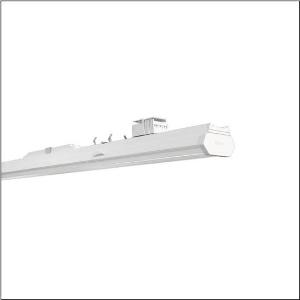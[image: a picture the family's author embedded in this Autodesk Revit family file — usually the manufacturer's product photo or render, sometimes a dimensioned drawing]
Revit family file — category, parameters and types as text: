
# Revit family: licross_r__21_protected_mo_52td12dn48xg_f2a3
name_source: partatom
category: Lighting Fixtures
units: mm (PartAtom-declared; Revit-internal decimal feet)

## family parameters
Cut with Voids When Loaded = No
Host = Face
Light Source = No
Part Type = Normal
Room Calculation Point = No
Round Connector Dimension = Use Diameter
Shared = No

## types (1)
- --- (1 x LED, 8000 lm, 45.3 W, 4000K)
    Apparent Load = 45 VA
    CIE Flux Codes = 73 92 98 99 100
    Color Rendering = 80
    Color Temperature = 4000K
    Default Elevation = 1800 mm
    Description = Licross® 21 Protected MO, luminaire insert, of sheet steel, galvanised, coil coated, white, length: 1.500mm, width: 90mm, height: 103mm, LED rated luminous flux: 8.000lm, light colour: 840, SDCM (Standard Deviation of Colour Matching)MacAdam ≤ 3 SDCM (initial), control gear: DALI 2, with plug, 5-pole, with phase selection, mains connection: 220..240V, AC, 50/60Hz, rated input power: 45W, internal wiring halogen-free, primary light control with lens, of plastic, primary optical cover: cover, of PMMA, light emission: direct distribution, primary light characteristic: symmetric, protection rating (complete): IP54, insulation class (complete): insulation class I (protective earthing), certification: CE, ENEC, VDE, UKCA, protection symbol: D if used in an environment with non-conductive dust loads with corresponding accessories, impact resistance: IK06, permissible ambient temperature for indoor applications: -25..+45°C, corresponds to IFS (International Featured Standards) requirements for safety and quality in the food industry, reducing of maximum allowable ambient temperature of 5°C with ceiling mounting, LABS conformity tested according to VDMA 24364:2018-05, packaging unit: 1 piece
    Height = 92 mm
    Lamp = 1 x LED
    Lamp Light Flux = 8000 lm
    Lamp Power = 45.3 W
    Lamp count = 1
    Length = 1500 mm
    Luminous efficacy = 177 lm/W
    Manufacturer = Siteco
    ModVariant = No
    Model = 52TD12DN48XG
    Mounting Place = Ceiling
    Mounting Type = Pendant
    Number of Poles = 1
    OnlyDefault = Yes
    Power Factor = 1
    Product Name = Licross® 21 Protected MO
    Product group = luminaire insert | ceiling pendant
    ProductGroupID = 901
    Protection Class = Protection class I
    Protection Degree = IP 54
    RLX_Detail_Level = 1
    RLX_Emergency_Light_Flux = 0 lm
    RLX_Emergency_Type = 0
    RLX_Emergency_Type_DB = No
    RlxData = <blob elided: 24481 chars, md5=6ddddbc8>
    Socket = socket
    Standby Power = 0 W
    System Light Flux = 8000 lm
    System Power = 45 W
    Type Comments = factory setting: luminous flux: 100 % | dim-lin: 254 | 305 mA
    Type Image = l_1256148.jpg
    URL = http://relux.com
    VarID = @adj_132669
    Voltage = 0 V
    Weight = 0.00 kg
    Width = 88 mm

## geometry (parser evidence)
native form markers: Blend x4, Sweep x9
no freeform markers — native parametric forms only
